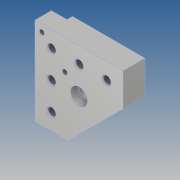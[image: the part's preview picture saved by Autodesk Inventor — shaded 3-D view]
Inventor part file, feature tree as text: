
AUTODESK INVENTOR PART (.ipt)
format: ipt  version: 2018.2 (Build 222227000, 227)  size: 168,448 bytes
history: native  units: mm
features: sketch x5, extrude x3, hole x3, other x1
ambient origin geometry x8: Origin, YZ Plane, XZ Plane, XY Plane, X Axis, Y Axis, Z Axis, Center Point
bodies: Body1 (feature_tree)
feature tree (12):
  extrude  "Grundkörper"  Depth=80.0mm
  extrude  "Abschnitt"  Depth=20.0mm TaperAngle=0.0deg
  hole  "DIN7984_M8"  [1 undecoded]
  extrude  "NUT_Torsionssicherung"  Depth=15.0mm
  hole  "M8_Profilgewinde"  [1 undecoded]
  hole  "M5_Bohrung"  [1 undecoded]
  other  "Basisskizze"
  sketch  "Skizze5"  dims[d2=80.0mm d3=30.0mm]
  sketch  "Skizze6"  dims[d4=30.0mm d17=20.0mm d18=0.0mm]
  sketch  "Skizze7"  dims[d19=30.0mm d20=30.0mm]
  sketch  "Skizze8"  dims[d21=15.0mm d22=0.0mm d23=40.0mm]
  sketch  "Skizze9"  dims[d24=21.213203mm d25=9.0mm d26=6.0mm d27=15.0mm d28=5.4mm d29=90.0deg d30=8.0mm d31=20.594885mm d32=20.0mm d33=5.0mm d34=0.0mm d38=15.0mm d39=15.0mm d41=30.0mm d43=25.0mm d44=10.0mm d46=10.0mm d48=25.0mm d49=25.0mm d50=6.647mm d51=16.0mm d52=8.0mm d53=5.4mm d54=90.0deg d55=22.2mm d56=20.594885mm d59=4.134mm d60=10.0mm d61=5.0mm d62=2.0mm d63=90.0deg d64=14.2mm d65=20.594885mm d72=18.0mm d73=47.5mm]
note: 3 required parameter values undecoded (feature->parameter linkage not recoverable at this tier; creation-order binding heuristic only, values carry confidence <= 0.55)
